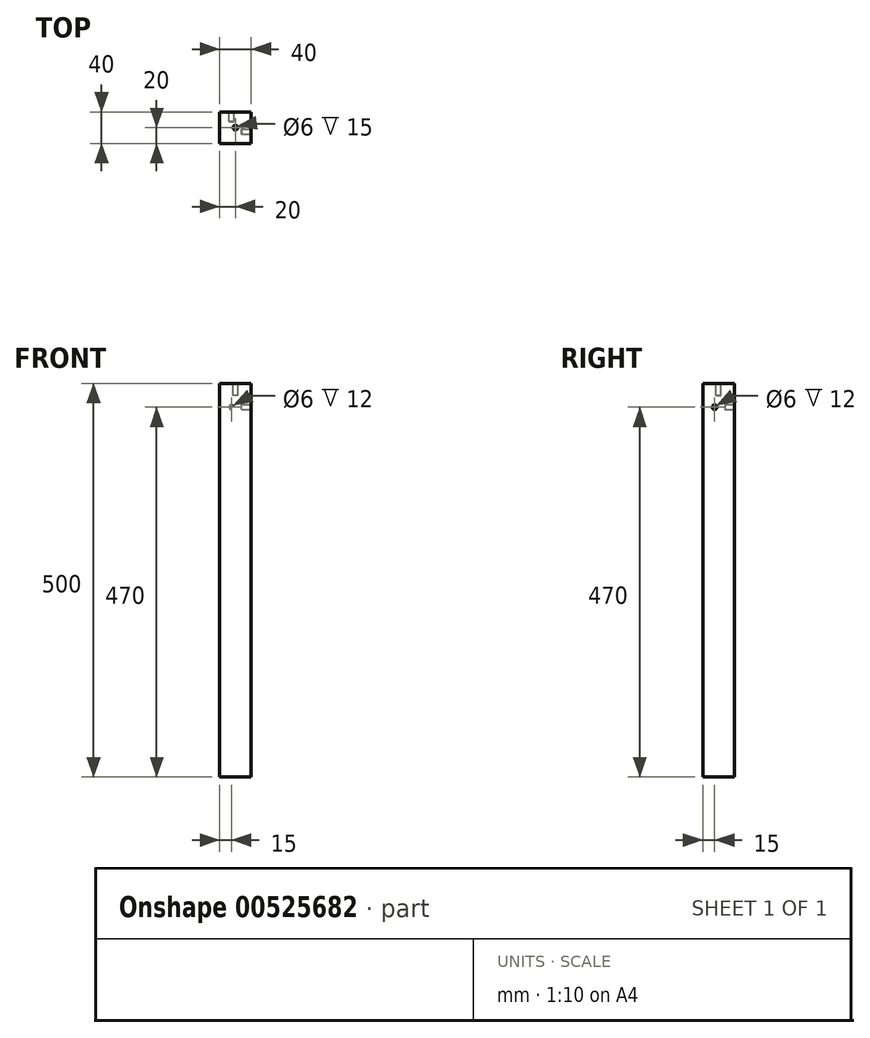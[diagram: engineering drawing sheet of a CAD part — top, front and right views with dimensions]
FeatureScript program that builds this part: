
annotation { "Feature Type Name" : "Feature", "Feature Type Description" : "" }
export const myFeature = defineFeature(function(context is Context, id is Id, definition is map)
    precondition{}
    {
        {
            var Q0;
            Q0=qCreatedBy(makeId("Top.planeOp"),FACE);
            var sketch = newSketch(context, id + "F0", { "sketchPlane" : qUnion([Q0])});
            skLineSegment(sketch, "E0.bottom", {"start": v(0, 0) * mm, "end": v(40, 0) * mm});
            skLineSegment(sketch, "E0.top", {"start": v(0, 40) * mm, "end": v(40, 40) * mm});
            skLineSegment(sketch, "E0.left", {"start": v(0, 0) * mm, "end": v(0, 40) * mm});
            skLineSegment(sketch, "E0.right", {"start": v(40, 0) * mm, "end": v(40, 40) * mm});
            skSolve(sketch);
        }
        {
            var Q0;
            Q0=qSketchRegion(id+"F0",true);
            extrude(context, id + "F1", {"entities" : qUnion([Q0]), "depth" : 500 * mm});
        }
        {
            var Q0;
            Q0=makeQuery(id+"F1.opExtrude","SWEPT_FACE",FACE,{"disambiguationData":[OSD([sQuery(id+"F0.wireOp",EDGE,"E0.right")])]});
            var sketch = newSketch(context, id + "F2", { "sketchPlane" : qUnion([Q0])});
            skCircle(sketch, "E1", {"center": v(15, 470) * mm, "radius": 3 * mm});
            skSolve(sketch);
        }
        {
            var Q0;
            Q0=qSketchRegion(id+"F2",true);
            extrude(context, id + "F3", {"entities" : qUnion([Q0]), "operationType" : NewBodyOperationType.REMOVE, "oppositeDirection" : true, "depth" : 12 * mm});
        }
        {
            var Q0;
            Q0=makeQuery(id+"F1.opExtrude","SWEPT_FACE",FACE,{"disambiguationData":[OSD([sQuery(id+"F0.wireOp",EDGE,"E0.top")])]});
            var sketch = newSketch(context, id + "F4", { "sketchPlane" : qUnion([Q0])});
            skCircle(sketch, "E2", {"center": v(-15, 470) * mm, "radius": 3 * mm});
            skSolve(sketch);
        }
        {
            var Q0;
            Q0=qSketchRegion(id+"F4",true);
            extrude(context, id + "F5", {"entities" : qUnion([Q0]), "operationType" : NewBodyOperationType.REMOVE, "oppositeDirection" : true, "depth" : 12 * mm});
        }
        {
            var Q0;
            Q0=makeQuery(id+"F1.opExtrude","CAP_FACE",FACE,{"disambiguationData":[OSD([sQuery(id+"F0.wireOp",EDGE,"E0.bottom"),sQuery(id+"F0.wireOp",EDGE,"E0.top"),sQuery(id+"F0.wireOp",EDGE,"E0.left"),sQuery(id+"F0.wireOp",EDGE,"E0.right")])],"isStart":false});
            var sketch = newSketch(context, id + "F6", { "sketchPlane" : qUnion([Q0])});
            skCircle(sketch, "E3", {"center": v(20, 20) * mm, "radius": 3 * mm});
            skSolve(sketch);
        }
        {
            var Q0;
            Q0=makeQuery(id+"F6.imprint","IMPRINT",FACE,{"disambiguationData":[TD([[makeQuery(id+"F6.imprint","IMPRINT",EDGE,{"derivedFrom":sQuery(id+"F6.wireOp",EDGE,"E3")}),1.0]])]});
            extrude(context, id + "F7", {"entities" : qUnion([Q0]), "operationType" : NewBodyOperationType.REMOVE, "oppositeDirection" : true, "depth" : 15 * mm, "offsetDistance" : 25 * mm});
        }
    });
